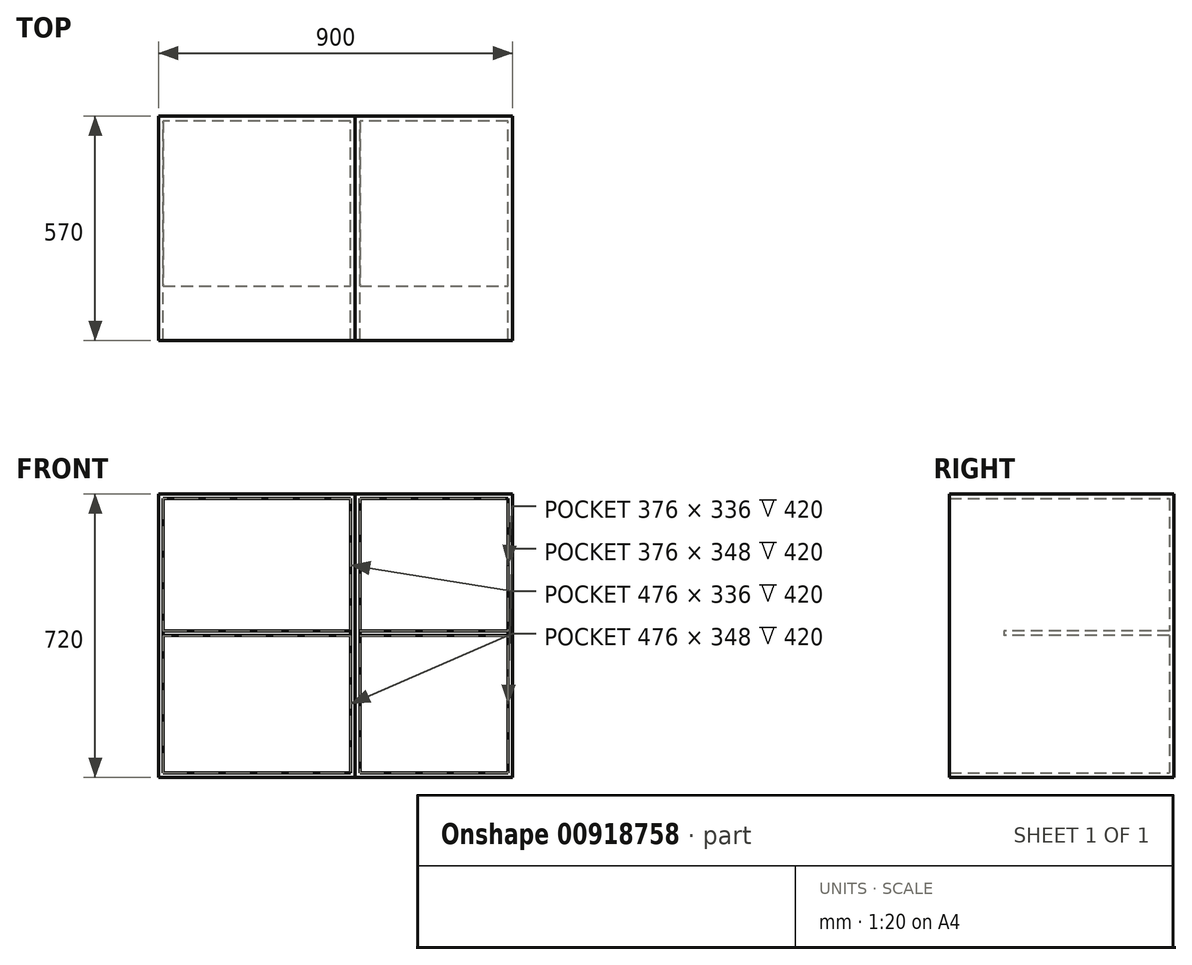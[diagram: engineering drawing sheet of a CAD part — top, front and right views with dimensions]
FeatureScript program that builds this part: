
annotation { "Feature Type Name" : "Feature", "Feature Type Description" : "" }
export const myFeature = defineFeature(function(context is Context, id is Id, definition is map)
    precondition{}
    {
        {
            var Q0;
            Q0=qCreatedBy(makeId("Top.planeOp"),FACE);
            var sketch = newSketch(context, id + "F0", { "sketchPlane" : qUnion([Q0])});
            skLineSegment(sketch, "E0.bottom", {"start": v(0, 0) * mm, "end": v(500, 0) * mm});
            skLineSegment(sketch, "E0.top", {"start": v(0, 570) * mm, "end": v(500, 570) * mm});
            skLineSegment(sketch, "E0.left", {"start": v(0, 0) * mm, "end": v(0, 570) * mm});
            skLineSegment(sketch, "E0.right", {"start": v(500, 0) * mm, "end": v(500, 570) * mm});
            skSolve(sketch);
        }
        {
            var Q0;
            Q0 = qSketchRegion(id + "F0", true);
            extrude(context, id + "F1", {"entities" : qUnion([Q0]), "depth" : 720 * mm, "offsetDistance" : 25 * mm});
        }
        {
            var Q0;
            Q0=makeQuery(id+"F1.opExtrude","SWEPT_FACE",FACE,{"disambiguationData":[OSD([sQuery(id+"F0.wireOp",EDGE,"E0.bottom")])]});
            shell(context, id + "F2", {"entities" : qUnion([Q0]), "thickness" : 12 * mm});
        }
        {
            var Q0;
            Q0=qCreatedBy(makeId("Top.planeOp"),FACE);
            cPlane(context, id + "F3", {"entities" : qUnion([Q0]), "cplaneType" : CPlaneType.OFFSET, "offset" : 360 * mm, "width" : 150 * mm, "height" : 150 * mm});
        }
        {
            var Q0;
            Q0=qCreatedBy(id+"F3.planeOp",FACE);
            var sketch = newSketch(context, id + "F4", { "sketchPlane" : qUnion([Q0])});
            skLineSegment(sketch, "E1.0.0", {"start": v(488, 558) * mm, "end": v(12, 558) * mm});
            skLineSegment(sketch, "E1.0.1", {"start": v(12, 558) * mm, "end": v(12, 138) * mm});
            skLineSegment(sketch, "E1.0.3", {"start": v(488, 138) * mm, "end": v(488, 558) * mm});
            skLineSegment(sketch, "E2", {"start": v(12, 138) * mm, "end": v(488, 138) * mm});
            skPoint(sketch, "E3.orphan", {"position": v(12, 0) * mm});
            skPoint(sketch, "E4.orphan", {"position": v(488, 0) * mm});
            skSolve(sketch);
        }
        {
            var Q0;
            Q0 = qSketchRegion(id + "F4", true);
            extrude(context, id + "F5", {"entities" : qUnion([Q0]), "operationType" : NewBodyOperationType.ADD, "depth" : 12 * mm, "offsetDistance" : 25 * mm});
        }
        {
            var Q0;
            Q0=makeQuery(id+"F1.opExtrude","SWEPT_FACE",FACE,{"disambiguationData":[OSD([sQuery(id+"F0.wireOp",EDGE,"E0.right")])]});
            extrude(context, id + "F6", {"entities" : qUnion([Q0]), "depth" : 400 * mm, "offsetDistance" : 25 * mm});
        }
        {
            var Q0;
            Q0=makeQuery(id+"F6.opExtrude","SWEPT_FACE",FACE,{"disambiguationData":[OSD([sQuery(id+"F0.wireOp",EDGE,"E0.bottom"),sQuery(id+"F0.wireOp",EDGE,"E0.right")])]});
            shell(context, id + "F7", {"entities" : qUnion([Q0]), "thickness" : 12 * mm});
        }
        {
            var Q0;
            Q0=qCreatedBy(id+"F3.planeOp",FACE);
            var sketch = newSketch(context, id + "F8", { "sketchPlane" : qUnion([Q0])});
            skLineSegment(sketch, "E5.0.0", {"start": v(512, 558) * mm, "end": v(512, 138) * mm});
            skLineSegment(sketch, "E5.0.2", {"start": v(888, 138) * mm, "end": v(888, 558) * mm});
            skLineSegment(sketch, "E5.0.3", {"start": v(888, 558) * mm, "end": v(512, 558) * mm});
            skLineSegment(sketch, "E6", {"start": v(512, 138) * mm, "end": v(888, 138) * mm});
            skPoint(sketch, "E5.0.1.end.orphan", {"position": v(888, 0) * mm});
            skPoint(sketch, "E5.0.1.start.orphan", {"position": v(512, 0) * mm});
            skSolve(sketch);
        }
        {
            var Q0;
            Q0 = qSketchRegion(id + "F8", true);
            var Q1;
            Q1=makeQuery(id+"F5.opExtrude","CAP_FACE",FACE,{"disambiguationData":[OSD([sQuery(id+"F4.wireOp",EDGE,"E1.0.0"),sQuery(id+"F4.wireOp",EDGE,"E1.0.1"),sQuery(id+"F4.wireOp",EDGE,"E1.0.3"),sQuery(id+"F4.wireOp",EDGE,"E2")])],"isStart":false});
            extrude(context, id + "F9", {"entities" : qUnion([Q0]), "operationType" : NewBodyOperationType.ADD, "endBound" : BoundingType.UP_TO_SURFACE, "depth" : 25 * mm, "endBoundEntityFace" : qUnion([Q1]), "offsetDistance" : 25 * mm});
        }
    });
